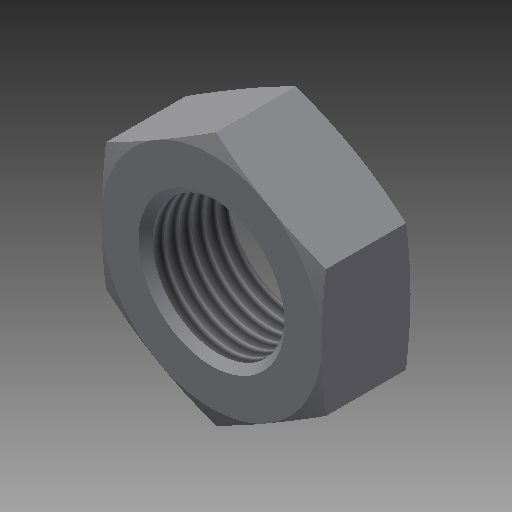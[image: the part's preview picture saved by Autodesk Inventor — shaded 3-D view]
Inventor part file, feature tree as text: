
AUTODESK INVENTOR PART (.ipt)
format: ipt  version: 2019 (Build 230136000, 136)  size: 184,832 bytes
history: native  units: in
note: dims shown in document units (in); Inventor stores cm internally (conversion verified against a paired STEP export)
features: other x70, sketch x3, revolve x2, extrude x1, thread x1
ambient origin geometry x8: Origin, YZ Plane, XZ Plane, XY Plane, X Axis, Y Axis, Z Axis, Center Point
bodies: Solid1 (feature_tree)
feature tree (77):
  sketch  "Sketch_8"  dims[d0=360.0deg d1=0.38in d2=0.0in]
  sketch  "Sketch_10"  dims[d3=360.0deg d4=0.3199in d5=0.0in]
  revolve  "Revolution1"  [1 undecoded]
  extrude  "Extrusion1"  Depth=0.3199in TaperAngle=0.0deg
  revolve  "Revolution2"  [1 undecoded]
  thread  "Thread1"  [1 undecoded]
  other  "NUT_XY"
  other  "NUT_YZ"
  other  "NUT_ZX"
  other  "NUT_X"
  other  "NUT_Y"
  other  "NUT_Z"
  other  "NUT_Center"
  other  "a1_XY"
  other  "a1_YZ"
  other  "a1_ZX"
  other  "a1_X"
  other  "a1_Y"
  other  "a1_Z"
  other  "a1_Center"
  other  "a2_XY"
  other  "a2_YZ"
  other  "a2_ZX"
  other  "a2_X"
  other  "a2_Y"
  other  "a2_Z"
  other  "a2_Center"
  other  "b1_XY"
  other  "b1_YZ"
  other  "b1_ZX"
  other  "b1_X"
  other  "b1_Y"
  other  "b1_Z"
  other  "b1_Center"
  other  "b2_XY"
  other  "b2_YZ"
  other  "b2_ZX"
  other  "b2_X"
  other  "b2_Y"
  other  "b2_Z"
  other  "b2_Center"
  other  "e_XY"
  other  "e_YZ"
  other  "e_ZX"
  other  "e_X"
  other  "e_Y"
  other  "e_Z"
  other  "e_Center"
  other  "ol1_XY"
  other  "ol1_YZ"
  other  "ol1_ZX"
  other  "ol1_X"
  other  "ol1_Y"
  other  "ol1_Z"
  other  "ol1_Center"
  other  "ol2_XY"
  other  "ol2_YZ"
  other  "ol2_ZX"
  other  "ol2_X"
  other  "ol2_Y"
  other  "ol2_Z"
  other  "ol2_Center"
  other  "th1_XY"
  other  "th1_YZ"
  other  "th1_ZX"
  other  "th1_X"
  other  "th1_Y"
  other  "th1_Z"
  other  "th1_Center"
  other  "th2_XY"
  other  "th2_YZ"
  other  "th2_ZX"
  other  "th2_X"
  other  "th2_Y"
  other  "th2_Z"
  other  "th2_Center"
  sketch  "Sketch_11"  dims[d6=0.0in d7=0.0in d8=0.0in]
note: 3 required parameter values undecoded (feature->parameter linkage not recoverable at this tier; creation-order binding heuristic only, values carry confidence <= 0.55)